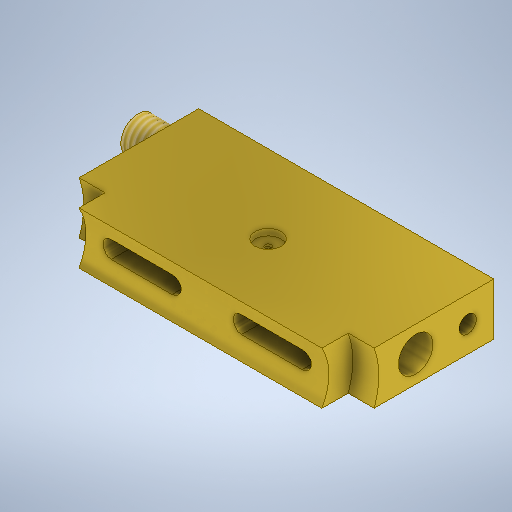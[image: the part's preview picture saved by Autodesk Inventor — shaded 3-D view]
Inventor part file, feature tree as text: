
AUTODESK INVENTOR PART (.ipt)
format: ipt  version: 2025.1 (Build 291241000, 241)  size: 374,272 bytes
history: native  units: mm
features: sketch x10, extrude x5, hole x5, mirror x2, plane x1, thread x1, projected_geometry x1
ambient origin geometry x8: Origin, YZ Plane, XZ Plane, XY Plane, X Axis, Y Axis, Z Axis, Center Point
bodies: Solid1 (feature_tree)
feature tree (25):
  extrude  "Extrusion1"  Depth=28.0mm
  plane  "Work Plane3"
  extrude  "Extrusion5"  Depth=68.0mm
  hole  "Hole1"  [1 undecoded]
  hole  "Hole6"  [1 undecoded]
  hole  "Hole3"  [1 undecoded]
  hole  "Hole4"  [1 undecoded]
  hole  "Hole5"  [1 undecoded]
  extrude  "Extrusion4"  Depth=8.0mm
  mirror  "Mirror2"
  extrude  "Extrusion2"  Depth=12.0mm TaperAngle=0.0deg
  extrude  "Extrusion3"  Depth=8.0mm
  mirror  "Mirror1"
  thread  "Thread1"  [1 undecoded]
  sketch  "Sketch1"  dims[d0=28.0mm d1=28.0mm]
  sketch  "Sketch2"  dims[d2=68.0mm d3=36.0mm]
  sketch  "Sketch4"  dims[d4=4.5mm d5=12.0mm d6=0.0mm]
  sketch  "Sketch5"  dims[d7=18.0mm]
  sketch  "Sketch6"  dims[d8=1.5mm d9=6.0mm d10=6.0mm d11=1.5mm d12=90.0deg d13=11.0mm d14=0.0mm d23=12.0mm]
  sketch  "Sketch7"  dims[d24=8.0mm d25=10.0mm d26=4.0mm d27=2.0mm d28=90.0deg d29=8.0mm d30=0.0mm d31=12.0mm]
  projected_geometry  "Projected Loop1"
  sketch  "Sketch8"  dims[d32=12.0mm]
  sketch  "Sketch10"  dims[d33=4.0mm d34=16.0mm d35=4.0mm d36=2.0mm d37=90.0deg d38=8.0mm d39=0.0mm d40=8.0mm]
  sketch  "Sketch12"  dims[d41=8.0mm]
  sketch  "Sketch13"  dims[d42=4.0mm d43=6.0mm d44=4.0mm d45=2.0mm d46=90.0deg d47=14.5mm d48=0.0mm d49=24.0mm d50=26.0mm d51=12.0mm d52=0.0mm d53=35.0mm d54=10.0mm d55=0.0mm d57=8.0mm d58=0.0mm d60=-28.0mm d61=8.0mm d62=6.0mm d63=14.0mm d64=0.0mm d65=4.0mm d66=10.0mm d67=5.0mm d68=9.0mm d69=90.0deg d70=8.0mm d71=0.0mm d72=8.0mm d73=0.0mm]
note: 6 required parameter values undecoded (feature->parameter linkage not recoverable at this tier; creation-order binding heuristic only, values carry confidence <= 0.55)
